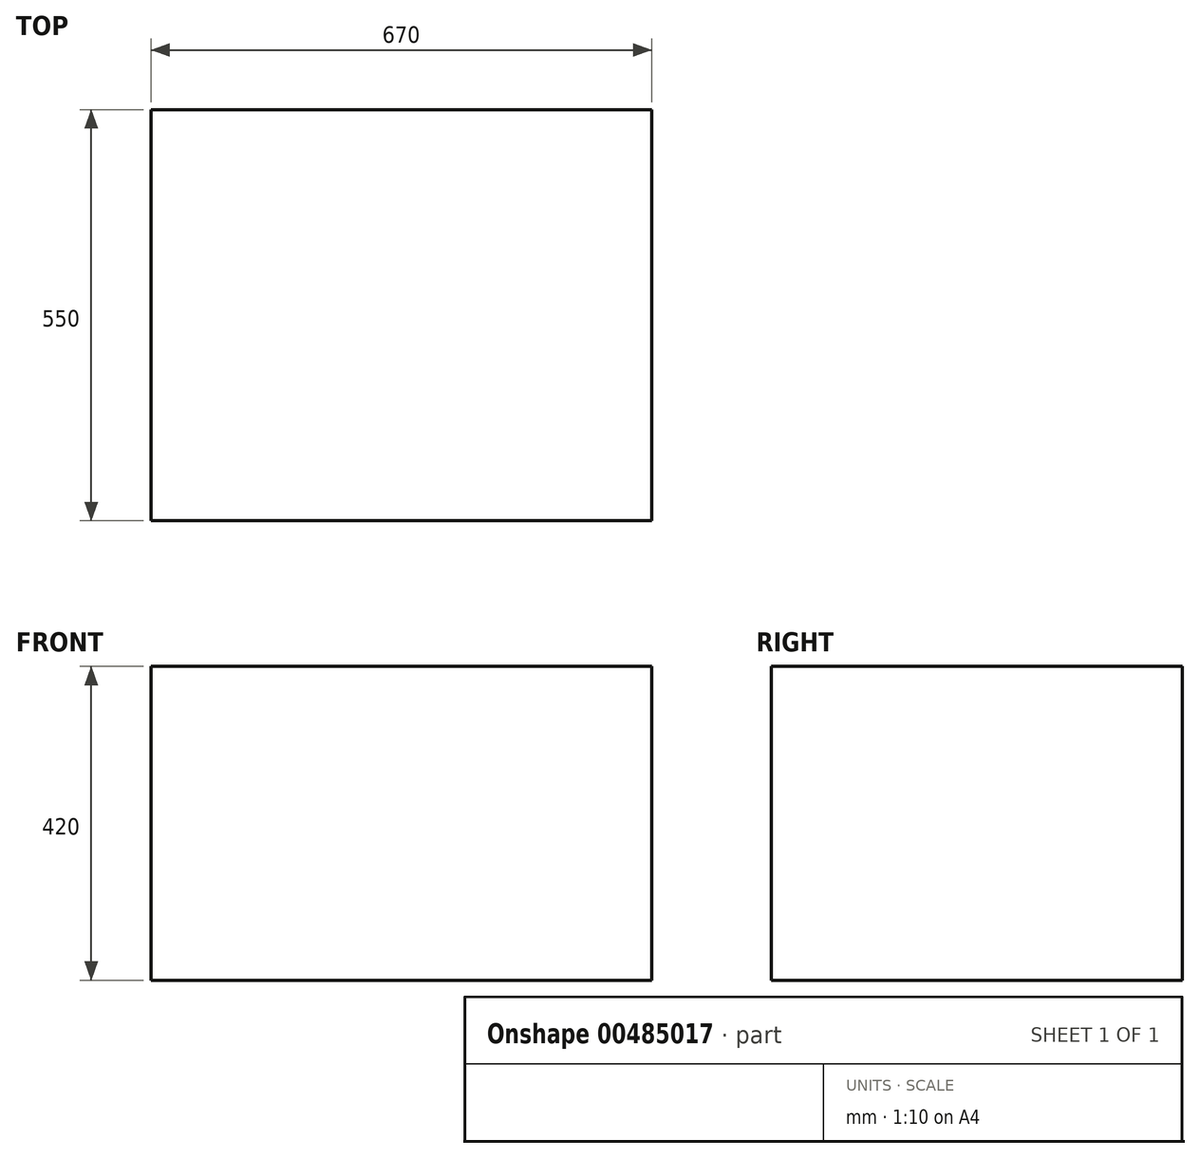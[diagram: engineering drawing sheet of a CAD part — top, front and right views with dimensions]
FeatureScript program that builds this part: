
annotation { "Feature Type Name" : "Feature", "Feature Type Description" : "" }
export const myFeature = defineFeature(function(context is Context, id is Id, definition is map)
    precondition{}
    {
        {
            var Q0;
            Q0=qCreatedBy(makeId("Top.planeOp"),FACE);
            var sketch = newSketch(context, id + "F0", { "sketchPlane" : qUnion([Q0])});
            skLineSegment(sketch, "E0.bottom", {"start": v(335, 275) * mm, "end": v(-335, 275) * mm});
            skLineSegment(sketch, "E0.top", {"start": v(335, -275) * mm, "end": v(-335, -275) * mm});
            skLineSegment(sketch, "E0.left", {"start": v(335, 275) * mm, "end": v(335, -275) * mm});
            skLineSegment(sketch, "E0.right", {"start": v(-335, 275) * mm, "end": v(-335, -275) * mm});
            skPoint(sketch, "E0.middle", {"position": v(0, 0) * mm});
            skSolve(sketch);
        }
        {
            var Q0;
            Q0=makeQuery(id+"F0.imprint","IMPRINT",FACE,{"disambiguationData":[TD([[makeQuery(id+"F0.imprint","IMPRINT",EDGE,{"derivedFrom":sQuery(id+"F0.wireOp",EDGE,"E0.bottom")}),1.0]])]});
            extrude(context, id + "F1", {"entities" : qUnion([Q0]), "depth" : 420 * mm, "offsetDistance" : 25 * mm});
        }
    });
